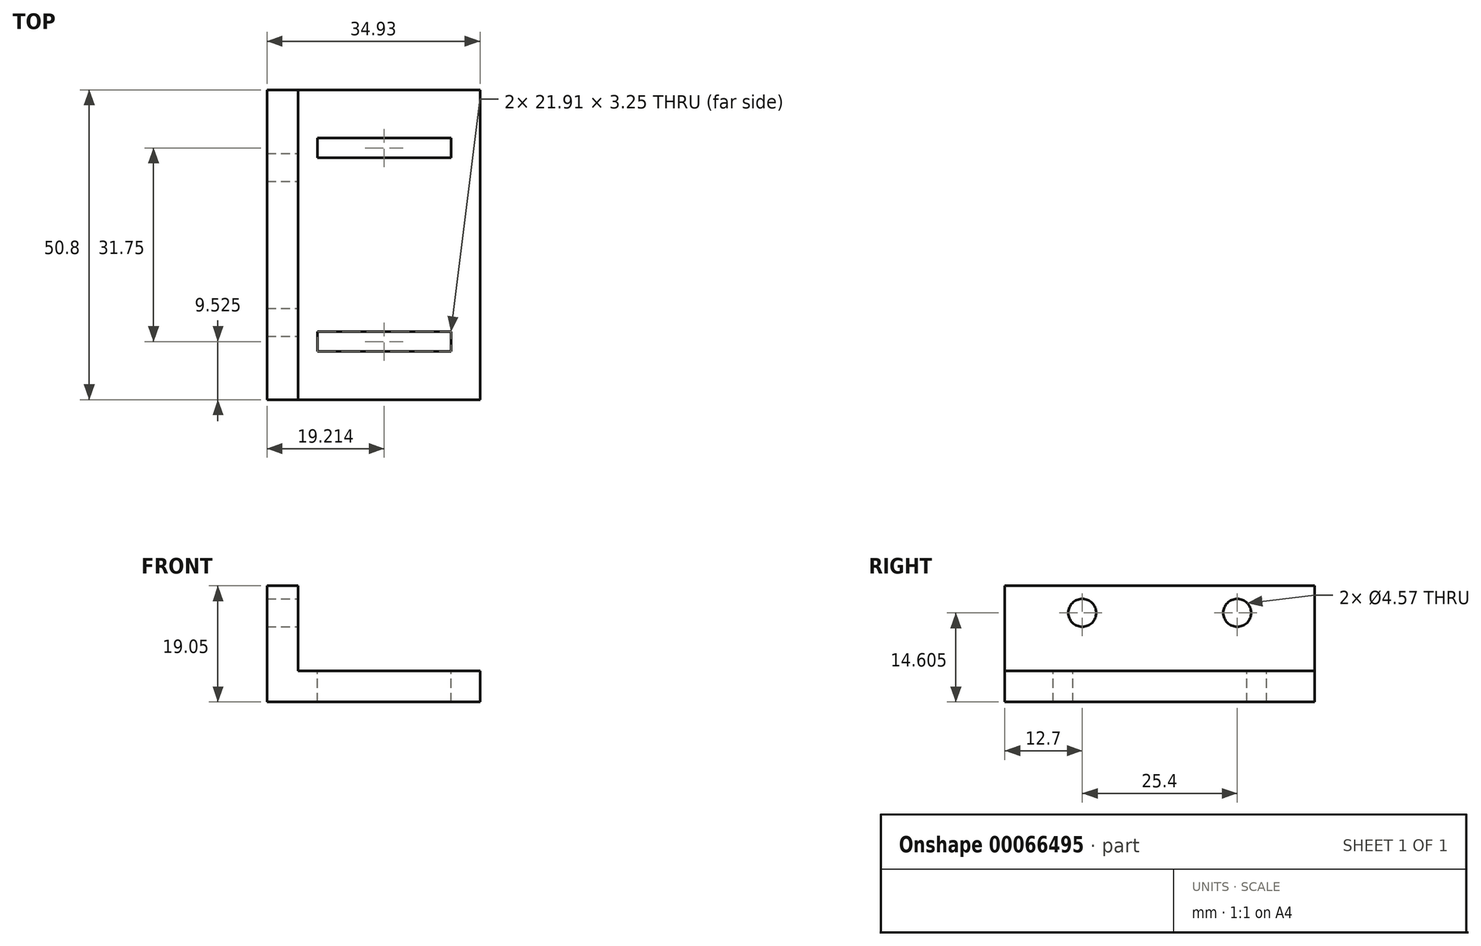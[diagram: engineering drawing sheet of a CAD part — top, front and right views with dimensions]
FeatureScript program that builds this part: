
annotation { "Feature Type Name" : "Feature", "Feature Type Description" : "" }
export const myFeature = defineFeature(function(context is Context, id is Id, definition is map)
    precondition{}
    {
        {
            var Q0;
            Q0=qCreatedBy(makeId("Front.planeOp"),FACE);
            var sketch = newSketch(context, id + "F0", { "sketchPlane" : qUnion([Q0])});
            skLineSegment(sketch, "E0", {"start": v(0, 0) * mm, "end": v(-34.93, 0) * mm});
            skLineSegment(sketch, "E1", {"start": v(-34.93, 0) * mm, "end": v(-34.93, 19.05) * mm});
            skLineSegment(sketch, "E2", {"start": v(-34.93, 19.05) * mm, "end": v(-29.85, 19.05) * mm});
            skLineSegment(sketch, "E3", {"start": v(-29.85, 19.05) * mm, "end": v(-29.85, 5.08) * mm});
            skLineSegment(sketch, "E4", {"start": v(-29.85, 5.08) * mm, "end": v(0, 5.08) * mm});
            skLineSegment(sketch, "E5", {"start": v(0, 5.08) * mm, "end": v(0, 0) * mm});
            skSolve(sketch);
        }
        {
            var Q0;
            Q0 = qSketchRegion(id + "F0", true);
            extrude(context, id + "F1", {"entities" : qUnion([Q0]), "depth" : 50.8 * mm});
        }
        {
            var Q0;
            Q0=makeQuery(id+"F1.opExtrude","SWEPT_FACE",FACE,{"disambiguationData":[OSD([sQuery(id+"F0.wireOp",EDGE,"E4")])]});
            var sketch = newSketch(context, id + "F2", { "sketchPlane" : qUnion([Q0])});
            skLineSegment(sketch, "E6.bottom", {"start": v(-26.67, -42.9) * mm, "end": v(-4.76, -42.9) * mm});
            skLineSegment(sketch, "E6.top", {"start": v(-26.67, -39.65) * mm, "end": v(-4.76, -39.65) * mm});
            skLineSegment(sketch, "E6.left", {"start": v(-26.67, -42.9) * mm, "end": v(-26.67, -39.65) * mm});
            skLineSegment(sketch, "E6.right", {"start": v(-4.76, -42.9) * mm, "end": v(-4.76, -39.65) * mm});
            skLineSegment(sketch, "E7.bottom", {"start": v(-26.67, -11.15) * mm, "end": v(-4.76, -11.15) * mm});
            skLineSegment(sketch, "E7.top", {"start": v(-26.67, -7.9) * mm, "end": v(-4.76, -7.9) * mm});
            skLineSegment(sketch, "E7.left", {"start": v(-26.67, -11.15) * mm, "end": v(-26.67, -7.9) * mm});
            skLineSegment(sketch, "E7.right", {"start": v(-4.76, -11.15) * mm, "end": v(-4.76, -7.9) * mm});
            skPoint(sketch, "E8", {"position": v(-4.76, -41.28) * mm});
            skPoint(sketch, "E9", {"position": v(-4.76, -9.52) * mm});
            skSolve(sketch);
        }
        {
            var Q0;
            Q0 = qSketchRegion(id + "F2", true);
            extrude(context, id + "F3", {"entities" : qUnion([Q0]), "operationType" : NewBodyOperationType.REMOVE, "oppositeDirection" : true, "depth" : 25.4 * mm});
        }
        {
            var Q0;
            Q0=makeQuery(id+"F1.opExtrude","SWEPT_FACE",FACE,{"disambiguationData":[OSD([sQuery(id+"F0.wireOp",EDGE,"E3")])]});
            var sketch = newSketch(context, id + "F4", { "sketchPlane" : qUnion([Q0])});
            skCircle(sketch, "E10", {"center": v(-38.1, 14.6) * mm, "radius": 2.29 * mm});
            skCircle(sketch, "E11", {"center": v(-12.7, 14.6) * mm, "radius": 2.29 * mm});
            skSolve(sketch);
        }
        {
            var Q0;
            Q0 = qSketchRegion(id + "F4", true);
            extrude(context, id + "F5", {"entities" : qUnion([Q0]), "operationType" : NewBodyOperationType.REMOVE, "oppositeDirection" : true, "depth" : 25.4 * mm});
        }
    });
